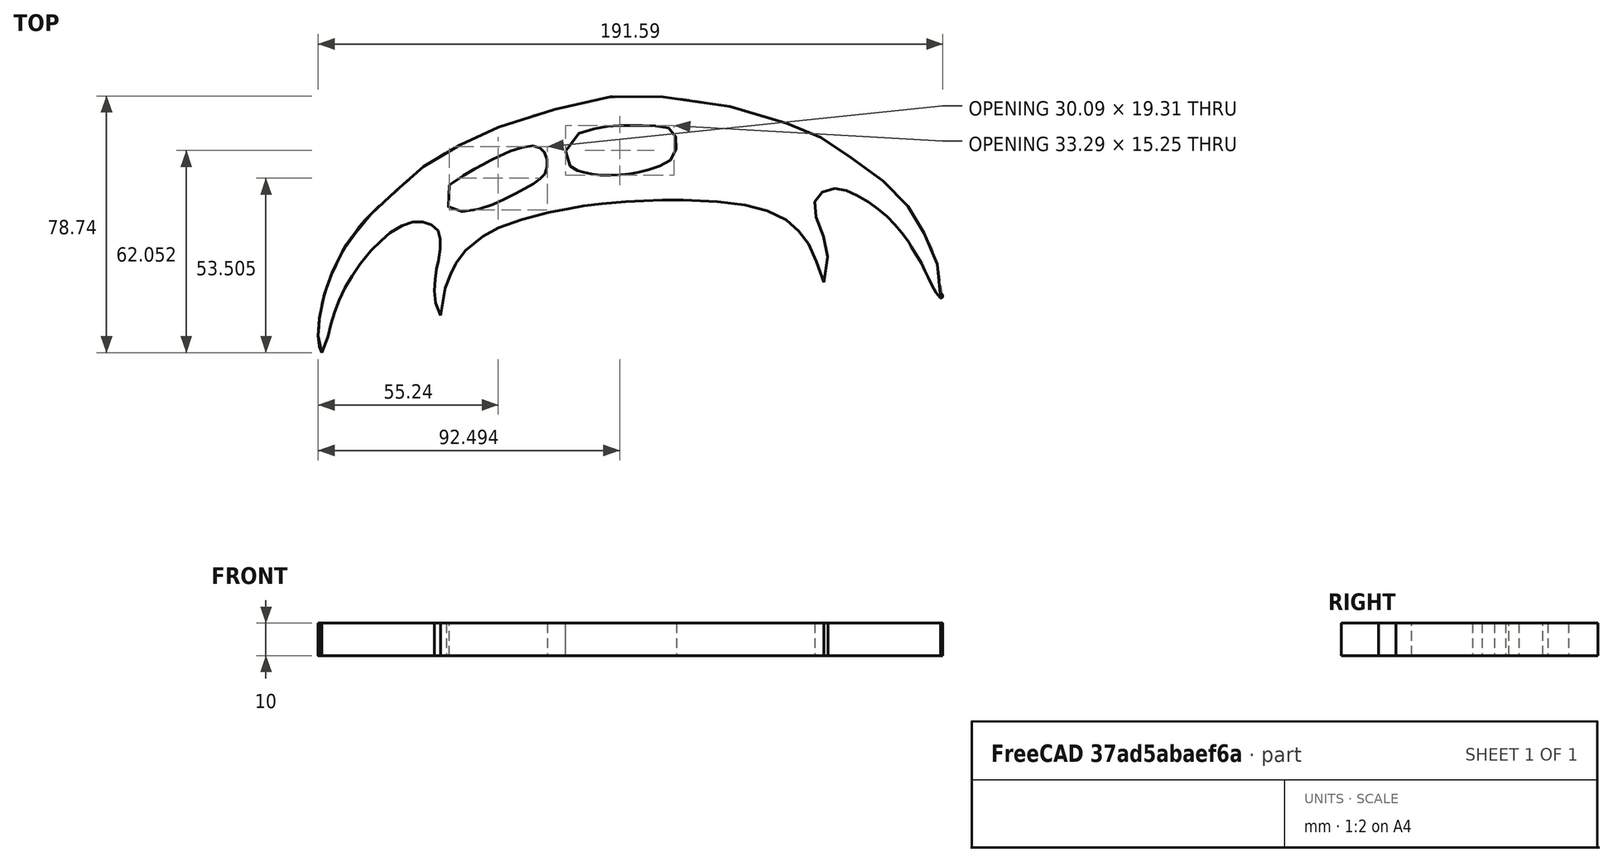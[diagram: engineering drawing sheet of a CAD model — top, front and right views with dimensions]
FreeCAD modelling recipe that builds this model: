
FCSTD DOCUMENT  (FreeCAD 0.19R24291 (Git))
Label: Batleth
License: All rights reserved
LicenseURL: http://en.wikipedia.org/wiki/All_rights_reserved
objects: Image::ImagePlane×1, Sketcher::SketchObject×1, PartDesign::Pad×1, PartDesign::Body×1
note: 4 computed .brp shape members not serialized (recipe doc carries the construction recipe); baked Part::Feature solids carry a one-line shape summary decoded from their .brp

FEATURE [Image::ImagePlane] ImagePlane
  XSize = 199
  YSize = 149
FEATURE [Sketcher::SketchObject] Sketch
  FullyConstrained = false
  MapMode = 5
  Support = -> [XY_Plane001]
  sketch-geometry (580):
    g0-g43: Circle x44 (B-spline internal-alignment scaffolding for g44; pole/knot coordinates omitted)
    g44: BSplineCurve PolesCount=44 KnotsCount=42 Degree=3 IsPeriodic=0
    g45-g86: GeomPoint x42 (B-spline internal-alignment scaffolding for g44; pole/knot coordinates omitted)
    g87-g98: Circle x12 (B-spline internal-alignment scaffolding for g99; pole/knot coordinates omitted)
    g99: BSplineCurve PolesCount=12 KnotsCount=10 Degree=3 IsPeriodic=0
    g100-g109: GeomPoint x10 (B-spline internal-alignment scaffolding for g99; pole/knot coordinates omitted)
    g110-g154: Circle x45 (B-spline internal-alignment scaffolding for g155; pole/knot coordinates omitted)
    g155: BSplineCurve PolesCount=45 KnotsCount=43 Degree=3 IsPeriodic=0
    g156-g198: GeomPoint x43 (B-spline internal-alignment scaffolding for g155; pole/knot coordinates omitted)
    g199-g247: Circle x49 (B-spline internal-alignment scaffolding for g248; pole/knot coordinates omitted)
    g248: BSplineCurve PolesCount=49 KnotsCount=47 Degree=3 IsPeriodic=0
    g249-g295: GeomPoint x47 (B-spline internal-alignment scaffolding for g248; pole/knot coordinates omitted)
    g296-g418: Circle x123 (B-spline internal-alignment scaffolding for g419; pole/knot coordinates omitted)
    g419: BSplineCurve PolesCount=123 KnotsCount=121 Degree=3 IsPeriodic=0
    g420-g540: GeomPoint x121 (B-spline internal-alignment scaffolding for g419; pole/knot coordinates omitted)
    g541-g560: Circle x20 (B-spline internal-alignment scaffolding for g561; pole/knot coordinates omitted)
    g561: BSplineCurve PolesCount=20 KnotsCount=18 Degree=3 IsPeriodic=0
    g562-g579: GeomPoint x18 (B-spline internal-alignment scaffolding for g561; pole/knot coordinates omitted)
  constraints (72):
    c: Weight(g0) = 1
    c: Equal(g0, g1-g43) x43
    c: InternalAlignment(g0-g43 -> g44) x44
    c: InternalAlignment(g45-g86 -> g44) x42
    c: Weight(g87) = 1
    c: Equal(g87, g88-g98) x11
    c: Coincident(g98,g87)
    c: InternalAlignment(g87-g98 -> g99) x12
    c: InternalAlignment(g100-g109 -> g99) x10
    c: Coincident(g155,g44)
    c: Weight(g110) = 1
    c: Equal(g110, g111-g154) x44
    c: InternalAlignment(g110-g154 -> g155) x45
    c: InternalAlignment(g156-g198 -> g155) x43
    c: Coincident(g248,g44)
    c: Weight(g199) = 1
    c: Equal(g199, g200-g227) x28
    c: PointOnObject(g227,g226)
    c: Equal(g199,g228)
    c: PointOnObject(g228,g227)
    c: Equal(g199, g229-g240) x12
    c: PointOnObject(g240,g239)
    c: Equal(g199,g241)
    c: PointOnObject(g241,g240)
    c: Equal(g199,g242)
    c: Equal(g199,g243)
    c: Equal(g199,g244)
    c: PointOnObject(g244,g243)
    c: Equal(g199,g245)
    c: PointOnObject(g245,g244)
    c: Equal(g199,g246)
    c: Equal(g199,g247)
    c: InternalAlignment(g199-g247 -> g248) x49
    c: InternalAlignment(g249-g295 -> g248) x47
    c: Coincident(g419,g155)
    c: Weight(g296) = 1
    c: Equal(g296,g297)
    c: Equal(g296,g298)
    c: Equal(g296,g299)
    c: PointOnObject(g299,g298)
    c: Equal(g296, g300-g318) x19
    c: PointOnObject(g318,g317)
    c: Equal(g296,g319)
    c: PointOnObject(g319,g318)
    c: Equal(g296, g320-g325) x6
    c: PointOnObject(g325,g324)
    c: Equal(g296, g326-g329) x4
    c: PointOnObject(g329,g-1)
    c: Equal(g296, g330-g334) x5
    c: PointOnObject(g334,g333)
    c: Equal(g296,g335)
    c: Equal(g296,g336)
    c: PointOnObject(g336,g335)
    c: Equal(g296,g337)
    c: PointOnObject(g337,g336)
    c: Equal(g296, g338-g385) x48
    c: PointOnObject(g385,g384)
    c: Equal(g296,g386)
    c: PointOnObject(g386,g385)
    c: Equal(g296, g387-g416) x30
    c: PointOnObject(g416,g415)
    c: Equal(g296,g417)
    c: PointOnObject(g417,g416)
    c: Equal(g296,g418)
    c: Coincident(g419,g248)
    c: InternalAlignment(g296-g418 -> g419) x123
    c: InternalAlignment(g420-g540 -> g419) x121
    c: Weight(g541) = 1
    c: Equal(g541, g542-g560) x19
    c: Coincident(g560,g541)
    c: InternalAlignment(g541-g560 -> g561) x20
    c: InternalAlignment(g562-g579 -> g561) x18
FEATURE [PartDesign::Pad] Pad
  Direction = (1,1,1)
  Length = 10
  Length2 = 100
  Profile = -> Sketch
  Type = 0
FEATURE [PartDesign::Body] Body
  Group = -> [Sketch,Pad]
  Origin = -> Origin001
  Tip = -> Pad
